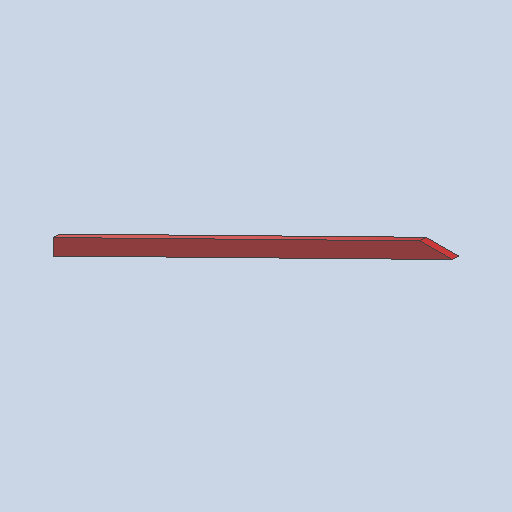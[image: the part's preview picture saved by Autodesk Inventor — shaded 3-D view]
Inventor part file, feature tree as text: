
AUTODESK INVENTOR PART (.ipt)
format: ipt  version: 2025.1 (Build 291241020, 241B)  size: 254,464 bytes
history: native  units: in
note: dims shown in document units (in); Inventor stores cm internally (conversion verified against a paired STEP export)
features: other x6, reference x3, extrude x1, sketch x1
ambient origin geometry x8: Origin, YZ Plane, XZ Plane, XY Plane, X Axis, Y Axis, Z Axis, Center Point
bodies: Solid1 (feature_tree)
feature tree (11):
  extrude  "Extrusion1"  Depth=1.5in TaperAngle=0.0deg
  sketch  "Sketch1"  dims[d0=3.5in d1=1.5in d2=0.0in]
  reference  "Reference1"
  reference  "Reference2"
  reference  "Reference3"
  other  "<userpath>\Documents\Tburn24\layer1\layer1.iam"
  other  "layer1.iam"
  other  "16'x2x4:2"
  other  "10'x2x4:6"
  other  "12'x2x4:1"
  other  "Finish1"
